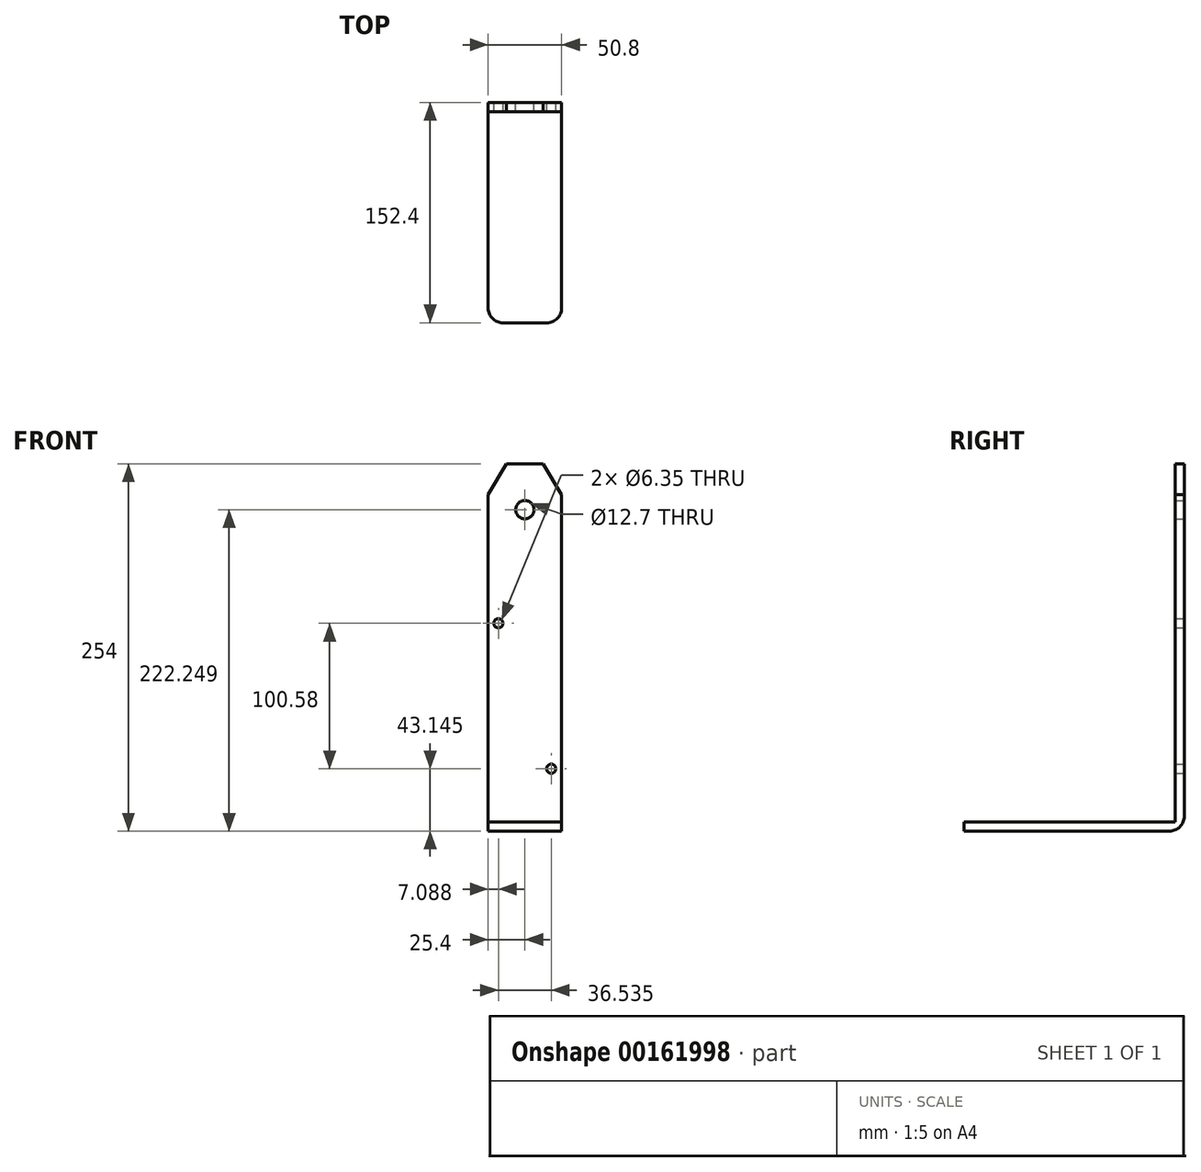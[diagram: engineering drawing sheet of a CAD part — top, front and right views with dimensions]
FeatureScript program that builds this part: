
annotation { "Feature Type Name" : "Feature", "Feature Type Description" : "" }
export const myFeature = defineFeature(function(context is Context, id is Id, definition is map)
    precondition{}
    {
        {
            var Q0;
            Q0=qCreatedBy(makeId("Front.planeOp"),FACE);
            var sketch = newSketch(context, id + "F0", { "sketchPlane" : qUnion([Q0])});
            skLineSegment(sketch, "E0", {"start": v(-25.4, 262.96) * mm, "end": v(-25.4, 30.26) * mm});
            skLineSegment(sketch, "E1", {"start": v(-25.4, 30.26) * mm, "end": v(25.4, 30.26) * mm});
            skLineSegment(sketch, "E2", {"start": v(25.4, 30.26) * mm, "end": v(25.4, 262.96) * mm});
            skLineSegment(sketch, "E3", {"start": v(-12.7, 284.26) * mm, "end": v(12.7, 284.26) * mm});
            skLineSegment(sketch, "E4", {"start": v(-25.4, 36.6) * mm, "end": v(25.4, 36.6) * mm});
            skLineSegment(sketch, "E5", {"start": v(-25.4, 262.96) * mm, "end": v(-12.7, 284.26) * mm});
            skLineSegment(sketch, "E6.MirrorCS", {"start": v(25.4, 262.96) * mm, "end": v(12.7, 284.26) * mm});
            skCircle(sketch, "E7", {"center": v(-18.31, 173.99) * mm, "radius": 3.18 * mm});
            skCircle(sketch, "E8", {"center": v(18.22, 73.4) * mm, "radius": 3.18 * mm});
            skLineSegment(sketch, "E9", {"start": v(0, 284.26) * mm, "end": v(0, 252.5) * mm});
            skPoint(sketch, "E9.endSnap0", {"position": v(0, 284.26) * mm});
            skCircle(sketch, "E10", {"center": v(0, 252.5) * mm, "radius": 6.35 * mm});
            skSolve(sketch);
        }
        {
            var Q0;
            {var subQ0=sQuery(id+"F0.wireOp",EDGE,"E1");Q0=makeQuery(id+"F0.imprint","IMPRINT",FACE,{"disambiguationData":[TD([[makeQuery(id+"F0.imprint","IMPRINT",EDGE,{"derivedFrom":subQ0}),1.0]])]});}
            extrude(context, id + "F1", {"entities" : qUnion([Q0]), "depth" : 152.4 * mm});
        }
        {
            var Q0;
            Q0=makeQuery(id+"F0.imprint","IMPRINT",FACE,{"disambiguationData":[TD([[makeQuery(id+"F0.imprint","IMPRINT",EDGE,{"derivedFrom":sQuery(id+"F0.wireOp",EDGE,"E3")}),-1.0]])]});
            extrude(context, id + "F2", {"entities" : qUnion([Q0]), "operationType" : NewBodyOperationType.ADD, "depth" : 6.35 * mm});
        }
        {
            var Q0;
            Q0=makeQuery(id+"F2.opExtrude","CAP_EDGE",EDGE,{"disambiguationData":[OSD([sQuery(id+"F0.wireOp",EDGE,"E4")])],"isStart":false});
            var Q1;
            Q1=makeQuery(id+"F1.opExtrude","CAP_EDGE",EDGE,{"disambiguationData":[OSD([sQuery(id+"F0.wireOp",EDGE,"E1")])],"isStart":true});
            fillet(context, id + "F3", {"entities" : qUnion([Q0, Q1]), "radius" : 10.16 * mm, "allowEdgeOverflow" : false});
        }
        {
            var Q0;
            Q0=makeQuery(id+"F1.opExtrude","CAP_EDGE",EDGE,{"disambiguationData":[OSD([sQuery(id+"F0.wireOp",EDGE,"E0")])],"isStart":false});
            var Q1;
            Q1=makeQuery(id+"F1.opExtrude","CAP_EDGE",EDGE,{"disambiguationData":[OSD([sQuery(id+"F0.wireOp",EDGE,"E2")])],"isStart":false});
            fillet(context, id + "F4", {"entities" : qUnion([Q0, Q1]), "radius" : 10.16 * mm, "tangentPropagation" : true, "allowEdgeOverflow" : false});
        }
    });
